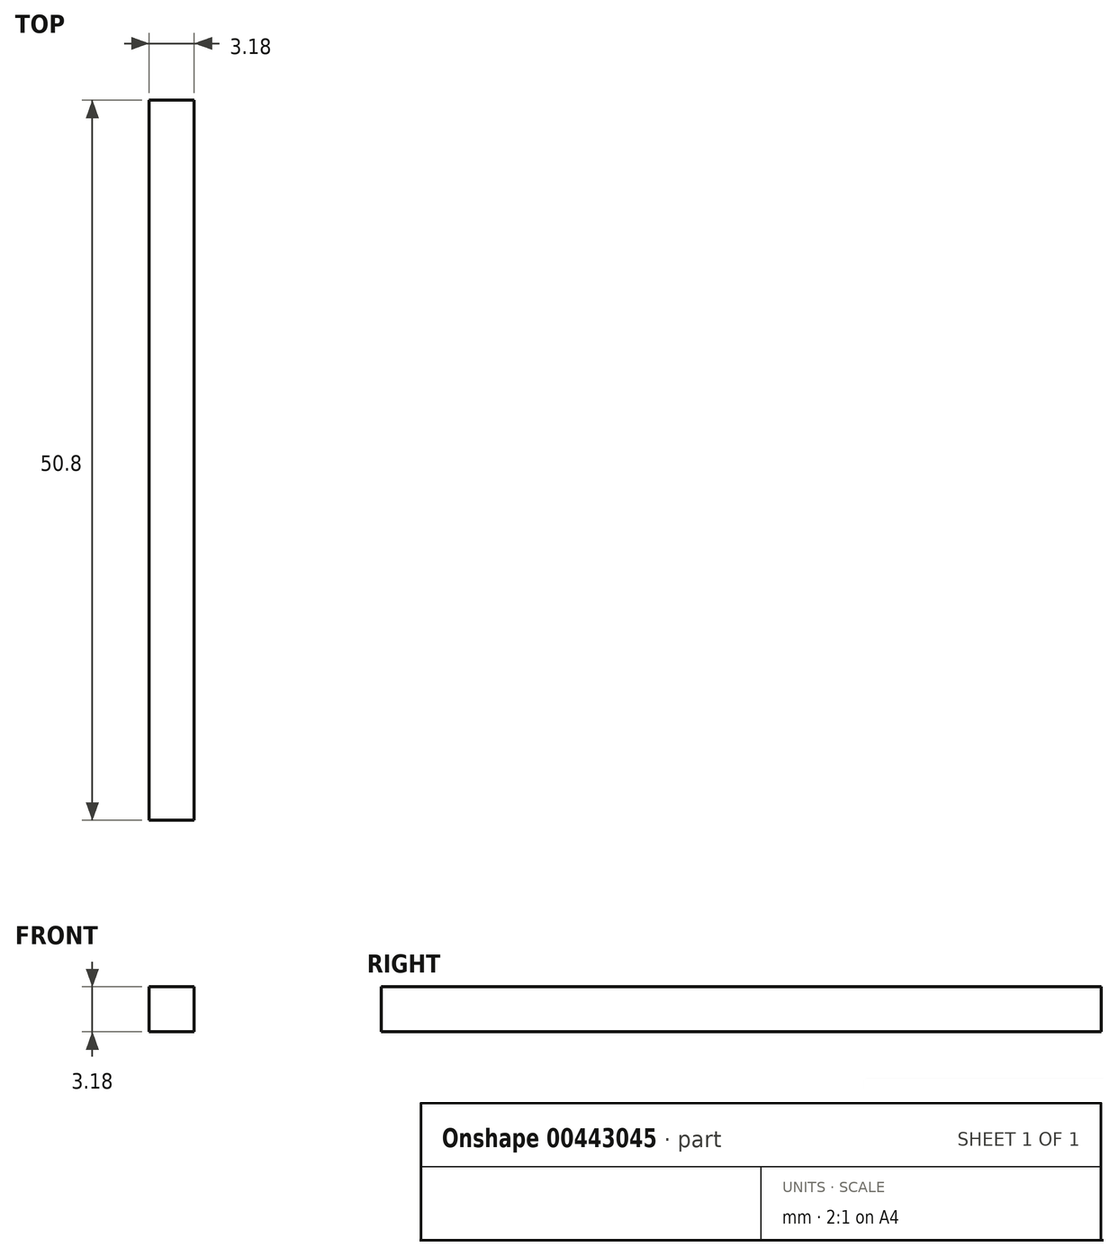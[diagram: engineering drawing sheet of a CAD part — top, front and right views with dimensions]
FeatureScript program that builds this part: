
annotation { "Feature Type Name" : "Feature", "Feature Type Description" : "" }
export const myFeature = defineFeature(function(context is Context, id is Id, definition is map)
    precondition{}
    {
        {
            var Q0;
            Q0=qCreatedBy(makeId("Front.planeOp"),FACE);
            var sketch = newSketch(context, id + "F0", { "sketchPlane" : qUnion([Q0])});
            skLineSegment(sketch, "E0.bottom", {"start": v(1.59, 1.59) * mm, "end": v(-1.59, 1.59) * mm});
            skLineSegment(sketch, "E0.top", {"start": v(1.59, -1.59) * mm, "end": v(-1.59, -1.59) * mm});
            skLineSegment(sketch, "E0.left", {"start": v(1.59, 1.59) * mm, "end": v(1.59, -1.59) * mm});
            skLineSegment(sketch, "E0.right", {"start": v(-1.59, 1.59) * mm, "end": v(-1.59, -1.59) * mm});
            skPoint(sketch, "E0.middle", {"position": v(0, 0) * mm});
            skSolve(sketch);
        }
        {
            var Q0;
            Q0=makeQuery(id+"F0.imprint","IMPRINT",FACE,{"disambiguationData":[TD([[makeQuery(id+"F0.imprint","IMPRINT",EDGE,{"derivedFrom":sQuery(id+"F0.wireOp",EDGE,"E0.bottom")}),1.0]])]});
            extrude(context, id + "F1", {"entities" : qUnion([Q0]), "endBound" : BoundingType.SYMMETRIC, "depth" : 50.8 * mm});
        }
    });
